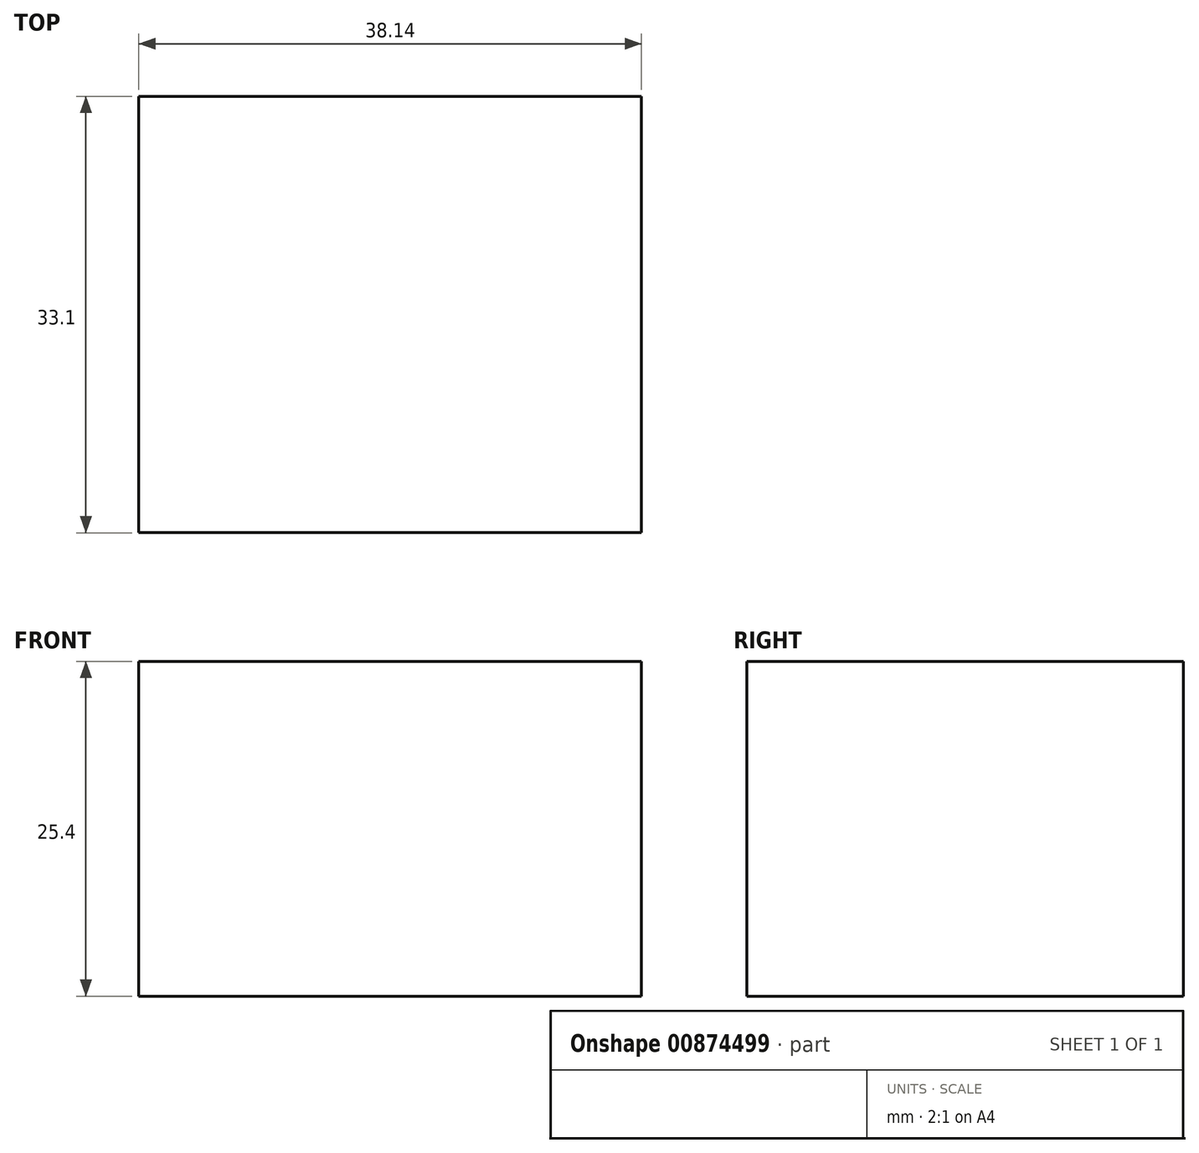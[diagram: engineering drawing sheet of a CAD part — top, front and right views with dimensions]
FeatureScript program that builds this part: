
annotation { "Feature Type Name" : "Feature", "Feature Type Description" : "" }
export const myFeature = defineFeature(function(context is Context, id is Id, definition is map)
    precondition{}
    {
        {
            var Q0;
            Q0=qCreatedBy(makeId("Top.planeOp"),FACE);
            var sketch = newSketch(context, id + "F0", { "sketchPlane" : qUnion([Q0])});
            skLineSegment(sketch, "E0.bottom", {"start": v(0, 0) * mm, "end": v(-38.14, 0) * mm});
            skLineSegment(sketch, "E0.top", {"start": v(0, -33.1) * mm, "end": v(-38.14, -33.1) * mm});
            skLineSegment(sketch, "E0.left", {"start": v(0, 0) * mm, "end": v(0, -33.1) * mm});
            skLineSegment(sketch, "E0.right", {"start": v(-38.14, 0) * mm, "end": v(-38.14, -33.1) * mm});
            skSolve(sketch);
        }
        {
            var Q0;
            Q0 = qSketchRegion(id + "F0", true);
            extrude(context, id + "F1", {"entities" : qUnion([Q0]), "depth" : 25.4 * mm, "offsetDistance" : 25.4 * mm});
        }
    });
